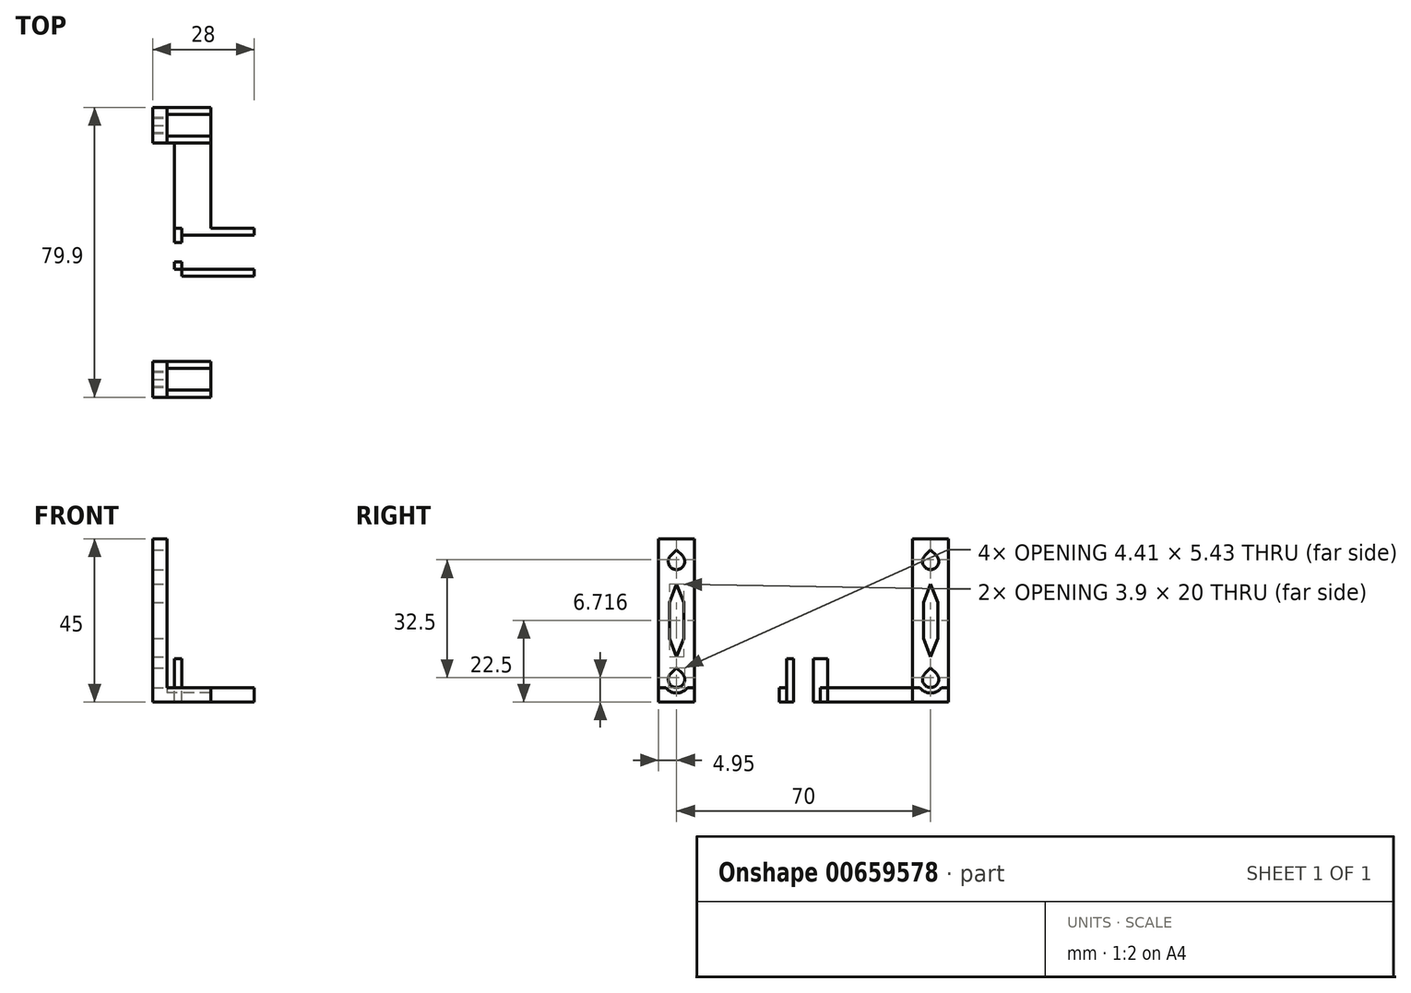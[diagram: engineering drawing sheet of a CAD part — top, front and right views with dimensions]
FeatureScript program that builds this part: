
annotation { "Feature Type Name" : "Feature", "Feature Type Description" : "" }
export const myFeature = defineFeature(function(context is Context, id is Id, definition is map)
    precondition{}
    {
        {
            var Q0;
            Q0=qCreatedBy(makeId("Right.planeOp"),FACE);
            var sketch = newSketch(context, id + "F0", { "sketchPlane" : qUnion([Q0])});
            skLineSegment(sketch, "E0.bottom", {"start": v(4.95, 6.25) * mm, "end": v(-4.95, 6.25) * mm});
            skLineSegment(sketch, "E0.top", {"start": v(4.95, -6.25) * mm, "end": v(-4.95, -6.25) * mm});
            skLineSegment(sketch, "E0.left", {"start": v(4.95, 6.25) * mm, "end": v(4.95, -6.25) * mm});
            skLineSegment(sketch, "E0.right", {"start": v(-4.95, 6.25) * mm, "end": v(-4.95, -6.25) * mm});
            skPoint(sketch, "E0.middle", {"position": v(0, 0) * mm});
            skCircle(sketch, "E1", {"center": v(0, 0) * mm, "radius": 2.25 * mm});
            skLineSegment(sketch, "E2", {"start": v(-4.95, 6.25) * mm, "end": v(-4.95, 16.25) * mm});
            skLineSegment(sketch, "E3", {"start": v(-4.95, 16.25) * mm, "end": v(-1.95, 16.25) * mm});
            skLineSegment(sketch, "E4", {"start": v(-1.95, 16.25) * mm, "end": v(-1.95, 6.25) * mm});
            skLineSegment(sketch, "E5", {"start": v(4.95, 6.25) * mm, "end": v(4.95, 16.25) * mm});
            skLineSegment(sketch, "E6", {"start": v(4.95, 16.25) * mm, "end": v(1.95, 16.25) * mm});
            skLineSegment(sketch, "E7", {"start": v(1.95, 16.25) * mm, "end": v(1.95, 6.25) * mm});
            skLineSegment(sketch, "E8", {"start": v(-4.95, -6.25) * mm, "end": v(-4.95, -2.25) * mm});
            skLineSegment(sketch, "E9", {"start": v(-4.95, -2.25) * mm, "end": v(4.95, -2.25) * mm});
            skLineSegment(sketch, "E10", {"start": v(4.95, -2.25) * mm, "end": v(4.95, -6.25) * mm});
            skLineSegment(sketch, "E11", {"start": v(0, 0) * mm, "end": v(35, 0) * mm});
            skPoint(sketch, "E11.endSnap0", {"position": v(4.95, 0) * mm});
            skCircle(sketch, "E12", {"center": v(0, 0) * mm, "radius": 3.75 * mm});
            skLineSegment(sketch, "E13", {"start": v(1.95, 11.25) * mm, "end": v(0, 6.25) * mm});
            skLineSegment(sketch, "E14", {"start": v(0, 6.25) * mm, "end": v(-1.95, 11.25) * mm});
            skSolve(sketch);
        }
        {
            var Q0;
            Q0=makeQuery(id+"F0.imprint","IMPRINT",FACE,{"disambiguationData":[TD([[makeQuery(id+"F0.imprint","IMPRINT",EDGE,{"derivedFrom":sQuery(id+"F0.wireOp",EDGE,"E0.bottom")}),1.0]])]});
            var Q1;
            {var subQ0=sQuery(id+"F0.wireOp",EDGE,"E2");Q1=makeQuery(id+"F0.imprint","IMPRINT",FACE,{"disambiguationData":[TD([[makeQuery(id+"F0.imprint","IMPRINT",EDGE,{"derivedFrom":subQ0}),-1.0]])]});}
            var Q2;
            {var subQ0=sQuery(id+"F0.wireOp",EDGE,"E5");Q2=makeQuery(id+"F0.imprint","IMPRINT",FACE,{"disambiguationData":[TD([[makeQuery(id+"F0.imprint","IMPRINT",EDGE,{"derivedFrom":subQ0}),1.0]])]});}
            var Q3;
            Q3=makeQuery(id+"F0.imprint","IMPRINT",FACE,{"disambiguationData":[TD([[makeQuery(id+"F0.imprint","IMPRINT",EDGE,{"derivedFrom":sQuery(id+"F0.wireOp",EDGE,"E0.top")}),-1.0]])]});
            var Q4;
            {var subQ1=sQuery(id+"F0.wireOp",EDGE,"E0.left");var subQ3=sQuery(id+"F0.wireOp",EDGE,"E11");var subQ4=makeQuery(id+"F0.imprint","INTERSECT",VERTEX,{"derivedFrom":[subQ1,subQ3]});Q4=makeQuery(id+"F0.imprint","IMPRINT",FACE,{"disambiguationData":[TD([[makeQuery(id+"F0.imprint","IMPRINT",EDGE,{"disambiguationData":[TD([[subQ4,1.0]])],"derivedFrom":subQ3}),-1.0]])]});}
            var Q5;
            {var subQ0=sQuery(id+"F0.wireOp",EDGE,"E9");var subQ1=makeQuery(id+"F0.imprint","INTERSECT",VERTEX,{"derivedFrom":[sQuery(id+"F0.wireOp",EDGE,"E1"),subQ0]});Q5=makeQuery(id+"F0.imprint","IMPRINT",FACE,{"disambiguationData":[TD([[makeQuery(id+"F0.imprint","IMPRINT",EDGE,{"disambiguationData":[TD([[subQ1,1.0]])],"derivedFrom":subQ0}),-1.0]])]});}
            var Q6;
            {var subQ0=sQuery(id+"F0.wireOp",EDGE,"E11");var subQ1=sQuery(id+"F0.wireOp",EDGE,"E1");var subQ2=makeQuery(id+"F0.imprint","INTERSECT",VERTEX,{"derivedFrom":[subQ1,subQ0]});Q6=makeQuery(id+"F0.imprint","IMPRINT",FACE,{"disambiguationData":[TD([[makeQuery(id+"F0.imprint","IMPRINT",EDGE,{"disambiguationData":[TD([[subQ2,-1.0]])],"derivedFrom":subQ1}),-1.0]])]});}
            var Q7;
            {var subQ0=sQuery(id+"F0.wireOp",EDGE,"E11");var subQ1=sQuery(id+"F0.wireOp",EDGE,"E1");var subQ2=makeQuery(id+"F0.imprint","INTERSECT",VERTEX,{"derivedFrom":[subQ1,subQ0]});Q7=makeQuery(id+"F0.imprint","IMPRINT",FACE,{"disambiguationData":[TD([[makeQuery(id+"F0.imprint","IMPRINT",EDGE,{"disambiguationData":[TD([[subQ2,1.0]])],"derivedFrom":subQ1}),-1.0]])]});}
            var Q8;
            {var subQ3=sQuery(id+"F0.wireOp",EDGE,"E14");Q8=makeQuery(id+"F0.imprint","IMPRINT",FACE,{"disambiguationData":[TD([[makeQuery(id+"F0.imprint","IMPRINT",EDGE,{"derivedFrom":subQ3}),1.0]])]});}
            var Q9;
            {var subQ3=sQuery(id+"F0.wireOp",EDGE,"E13");Q9=makeQuery(id+"F0.imprint","IMPRINT",FACE,{"disambiguationData":[TD([[makeQuery(id+"F0.imprint","IMPRINT",EDGE,{"derivedFrom":subQ3}),1.0]])]});}
            extrude(context, id + "F1", {"entities" : qUnion([Q0, Q1, Q2, Q3, Q4, Q5, Q6, Q7, Q8, Q9]), "oppositeDirection" : true, "depth" : 4 * mm, "offsetDistance" : 25 * mm});
        }
        {
            var Q0;
            Q0=makeQuery(id+"F0.imprint","IMPRINT",FACE,{"disambiguationData":[TD([[makeQuery(id+"F0.imprint","IMPRINT",EDGE,{"derivedFrom":sQuery(id+"F0.wireOp",EDGE,"E0.top")}),-1.0]])]});
            extrude(context, id + "F2", {"entities" : qUnion([Q0]), "depth" : 12 * mm, "offsetDistance" : 25 * mm});
        }
        {
            var Q0;
            Q0=makeQuery(id+"F1.opExtrude","SWEPT_FACE",FACE,{"disambiguationData":[OSD([sQuery(id+"F0.wireOp",EDGE,"E6")])]});
            cPlane(context, id + "F3", {"entities" : qUnion([Q0]), "cplaneType" : CPlaneType.OFFSET, "offset" : 0 * mm, "width" : 150 * mm, "height" : 150 * mm});
        }
        {
            var Q0;
            Q0=makeQuery(id+"F1.opExtrude","SWEPT_BODY",BODY,{"disambiguationData":[OSD([sQuery(id+"F0.wireOp",EDGE,"E0.bottom"),sQuery(id+"F0.wireOp",EDGE,"E0.top"),sQuery(id+"F0.wireOp",EDGE,"E0.left"),sQuery(id+"F0.wireOp",EDGE,"E0.right"),sQuery(id+"F0.wireOp",EDGE,"E1"),sQuery(id+"F0.wireOp",EDGE,"E2"),sQuery(id+"F0.wireOp",EDGE,"E3"),sQuery(id+"F0.wireOp",EDGE,"E4"),sQuery(id+"F0.wireOp",EDGE,"E5"),sQuery(id+"F0.wireOp",EDGE,"E6"),sQuery(id+"F0.wireOp",EDGE,"E7"),sQuery(id+"F0.wireOp",EDGE,"E8"),sQuery(id+"F0.wireOp",EDGE,"E10")])]});
            var Q1;
            Q1=qCreatedBy(id+"F3.planeOp",FACE);
            mirror(context, id + "F4", {"operationType" : NewBodyOperationType.ADD, "entities" : qUnion([Q0]), "mirrorPlane" : qUnion([Q1])});
        }
        {
            var Q0;
            Q0=sQuery(id+"F0.wireOp",VERTEX,"E11.end");
            var Q1;
            Q1=sQuery(id+"F0.wireOp",EDGE,"E11");
            cPlane(context, id + "F5", {"entities" : qUnion([Q0, Q1]), "cplaneType" : CPlaneType.LINE_POINT, "offset" : 25 * mm, "width" : 150 * mm, "height" : 150 * mm});
        }
        {
            var Q0;
            Q0=makeQuery(id+"F1.opExtrude","SWEPT_BODY",BODY,{"disambiguationData":[OSD([sQuery(id+"F0.wireOp",EDGE,"E0.bottom"),sQuery(id+"F0.wireOp",EDGE,"E0.top"),sQuery(id+"F0.wireOp",EDGE,"E0.left"),sQuery(id+"F0.wireOp",EDGE,"E0.right"),sQuery(id+"F0.wireOp",EDGE,"E1"),sQuery(id+"F0.wireOp",EDGE,"E2"),sQuery(id+"F0.wireOp",EDGE,"E3"),sQuery(id+"F0.wireOp",EDGE,"E4"),sQuery(id+"F0.wireOp",EDGE,"E5"),sQuery(id+"F0.wireOp",EDGE,"E6"),sQuery(id+"F0.wireOp",EDGE,"E7"),sQuery(id+"F0.wireOp",EDGE,"E8"),sQuery(id+"F0.wireOp",EDGE,"E10")])]});
            var Q1;
            Q1=makeQuery(id+"F2.opExtrude","SWEPT_BODY",BODY,{"disambiguationData":[OSD([sQuery(id+"F0.wireOp",EDGE,"E0.top"),sQuery(id+"F0.wireOp",EDGE,"E8"),sQuery(id+"F0.wireOp",EDGE,"E9"),sQuery(id+"F0.wireOp",EDGE,"E10")])]});
            var Q2;
            Q2=qCreatedBy(id+"F5.planeOp",FACE);
            mirror(context, id + "F6", {"entities" : qUnion([Q0, Q1]), "mirrorPlane" : qUnion([Q2])});
        }
        {
            var Q0;
            Q0=makeQuery(id+"F2.opExtrude","SWEPT_FACE",FACE,{"disambiguationData":[OSD([sQuery(id+"F0.wireOp",EDGE,"E9")])]});
            var sketch = newSketch(context, id + "F7", { "sketchPlane" : qUnion([Q0])});
            skPoint(sketch, "E15.0", {"position": v(0, 4.95) * mm});
            skPoint(sketch, "E16.0", {"position": v(0, 65.05) * mm});
            skPoint(sketch, "E17.0", {"position": v(12, 65.05) * mm});
            skPoint(sketch, "E18.0", {"position": v(12, 4.95) * mm});
            skLineSegment(sketch, "E19", {"start": v(0, 4.95) * mm, "end": v(2, 4.95) * mm});
            skLineSegment(sketch, "E20", {"start": v(2, 4.95) * mm, "end": v(2, 65.05) * mm});
            skLineSegment(sketch, "E21", {"start": v(2, 35) * mm, "end": v(2, 41.65) * mm});
            skLineSegment(sketch, "E22", {"start": v(2, 41.65) * mm, "end": v(2, 28.35) * mm});
            skLineSegment(sketch, "E23", {"start": v(2, 28.35) * mm, "end": v(24, 28.35) * mm});
            skLineSegment(sketch, "E24", {"start": v(24, 28.35) * mm, "end": v(24, 41.65) * mm});
            skLineSegment(sketch, "E25", {"start": v(24, 41.65) * mm, "end": v(2, 41.65) * mm});
            skLineSegment(sketch, "E26", {"start": v(24, 41.65) * mm, "end": v(24, 39.65) * mm});
            skLineSegment(sketch, "E27", {"start": v(24, 39.65) * mm, "end": v(2, 39.65) * mm});
            skLineSegment(sketch, "E28", {"start": v(24, 28.35) * mm, "end": v(24, 30.35) * mm});
            skLineSegment(sketch, "E29", {"start": v(24, 30.35) * mm, "end": v(2, 30.35) * mm});
            skLineSegment(sketch, "E30", {"start": v(2, 28.35) * mm, "end": v(4, 28.35) * mm});
            skLineSegment(sketch, "E31", {"start": v(4, 28.35) * mm, "end": v(4, 41.65) * mm});
            skLineSegment(sketch, "E32", {"start": v(2, 35) * mm, "end": v(2, 37.7) * mm});
            skLineSegment(sketch, "E33", {"start": v(2, 37.7) * mm, "end": v(4, 37.7) * mm});
            skLineSegment(sketch, "E34", {"start": v(2, 35) * mm, "end": v(2, 32.3) * mm});
            skLineSegment(sketch, "E35", {"start": v(2, 32.3) * mm, "end": v(4, 32.3) * mm});
            skLineSegment(sketch, "E36", {"start": v(12, 4.95) * mm, "end": v(12, 28.35) * mm});
            skPoint(sketch, "E36.endSnap0", {"position": v(13, 28.35) * mm});
            skLineSegment(sketch, "E37", {"start": v(12, 65.05) * mm, "end": v(12, 41.65) * mm});
            skPoint(sketch, "E37.endSnap0", {"position": v(13, 41.65) * mm});
            skLineSegment(sketch, "E38", {"start": v(12, 65.05) * mm, "end": v(2, 65.05) * mm});
            skSolve(sketch);
        }
        {
            var Q0;
            {var subQ1=sQuery(id+"F7.wireOp",EDGE,"E30");Q0=makeQuery(id+"F7.imprint","IMPRINT",FACE,{"disambiguationData":[TD([[makeQuery(id+"F7.imprint","IMPRINT",EDGE,{"derivedFrom":subQ1}),-1.0]])]});}
            var Q1;
            {var subQ0=sQuery(id+"F7.wireOp",EDGE,"E28");Q1=makeQuery(id+"F7.imprint","IMPRINT",FACE,{"disambiguationData":[TD([[makeQuery(id+"F7.imprint","IMPRINT",EDGE,{"derivedFrom":subQ0}),1.0]])]});}
            var Q2;
            {var subQ0=sQuery(id+"F7.wireOp",EDGE,"E30");Q2=makeQuery(id+"F7.imprint","IMPRINT",FACE,{"disambiguationData":[TD([[makeQuery(id+"F7.imprint","IMPRINT",EDGE,{"derivedFrom":subQ0}),1.0]])]});}
            var Q3;
            {var subQ3=sQuery(id+"F7.wireOp",EDGE,"E35");Q3=makeQuery(id+"F7.imprint","IMPRINT",FACE,{"disambiguationData":[TD([[makeQuery(id+"F7.imprint","IMPRINT",EDGE,{"derivedFrom":subQ3}),-1.0]])]});}
            var Q4;
            {var subQ3=sQuery(id+"F7.wireOp",EDGE,"E33");Q4=makeQuery(id+"F7.imprint","IMPRINT",FACE,{"disambiguationData":[TD([[makeQuery(id+"F7.imprint","IMPRINT",EDGE,{"derivedFrom":subQ3}),1.0]])]});}
            var Q5;
            {var subQ1=sQuery(id+"F7.wireOp",EDGE,"E22");var subQ3=sQuery(id+"F7.wireOp",EDGE,"E27");var subQ4=makeQuery(id+"F7.imprint","INTERSECT",VERTEX,{"derivedFrom":[subQ1,subQ3]});Q5=makeQuery(id+"F7.imprint","IMPRINT",FACE,{"disambiguationData":[TD([[makeQuery(id+"F7.imprint","IMPRINT",EDGE,{"disambiguationData":[TD([[subQ4,1.0]])],"derivedFrom":subQ3}),-1.0]])]});}
            var Q6;
            {var subQ1=sQuery(id+"F7.wireOp",EDGE,"E26");Q6=makeQuery(id+"F7.imprint","IMPRINT",FACE,{"disambiguationData":[TD([[makeQuery(id+"F7.imprint","IMPRINT",EDGE,{"derivedFrom":subQ1}),-1.0]])]});}
            var Q7;
            {var subQ0=sQuery(id+"F7.wireOp",EDGE,"E37");Q7=makeQuery(id+"F7.imprint","IMPRINT",FACE,{"disambiguationData":[TD([[makeQuery(id+"F7.imprint","IMPRINT",EDGE,{"derivedFrom":subQ0}),-1.0]])]});}
            var Q8;
            {var subQ4=sQuery(id+"F7.wireOp",EDGE,"E24");Q8=makeQuery(id+"F7.imprint","IMPRINT",FACE,{"disambiguationData":[TD([[makeQuery(id+"F7.imprint","IMPRINT",EDGE,{"derivedFrom":subQ4}),1.0]])]});}
            var Q9;
            Q9=makeQuery(id+"F7.imprint","IMPRINT",FACE,{"disambiguationData":[TD([[makeQuery(id+"F7.imprint","IMPRINT",EDGE,{"derivedFrom":sQuery(id+"F7.wireOp",EDGE,"E32")}),-1.0]])]});
            extrude(context, id + "F8", {"entities" : qUnion([Q0, Q1, Q2, Q3, Q4, Q5, Q6, Q7, Q8, Q9]), "oppositeDirection" : true, "depth" : 4 * mm, "offsetDistance" : 25 * mm});
        }
        {
            var Q0;
            {var subQ1=sQuery(id+"F7.wireOp",EDGE,"E26");Q0=makeQuery(id+"F7.imprint","IMPRINT",FACE,{"disambiguationData":[TD([[makeQuery(id+"F7.imprint","IMPRINT",EDGE,{"derivedFrom":subQ1}),-1.0]])]});}
            var Q1;
            {var subQ1=sQuery(id+"F7.wireOp",EDGE,"E22");var subQ3=sQuery(id+"F7.wireOp",EDGE,"E27");var subQ4=makeQuery(id+"F7.imprint","INTERSECT",VERTEX,{"derivedFrom":[subQ1,subQ3]});Q1=makeQuery(id+"F7.imprint","IMPRINT",FACE,{"disambiguationData":[TD([[makeQuery(id+"F7.imprint","IMPRINT",EDGE,{"disambiguationData":[TD([[subQ4,1.0]])],"derivedFrom":subQ3}),-1.0]])]});}
            var Q2;
            {var subQ3=sQuery(id+"F7.wireOp",EDGE,"E33");Q2=makeQuery(id+"F7.imprint","IMPRINT",FACE,{"disambiguationData":[TD([[makeQuery(id+"F7.imprint","IMPRINT",EDGE,{"derivedFrom":subQ3}),1.0]])]});}
            var Q3;
            {var subQ3=sQuery(id+"F7.wireOp",EDGE,"E35");Q3=makeQuery(id+"F7.imprint","IMPRINT",FACE,{"disambiguationData":[TD([[makeQuery(id+"F7.imprint","IMPRINT",EDGE,{"derivedFrom":subQ3}),-1.0]])]});}
            var Q4;
            {var subQ0=sQuery(id+"F7.wireOp",EDGE,"E30");Q4=makeQuery(id+"F7.imprint","IMPRINT",FACE,{"disambiguationData":[TD([[makeQuery(id+"F7.imprint","IMPRINT",EDGE,{"derivedFrom":subQ0}),1.0]])]});}
            var Q5;
            {var subQ0=sQuery(id+"F7.wireOp",EDGE,"E28");Q5=makeQuery(id+"F7.imprint","IMPRINT",FACE,{"disambiguationData":[TD([[makeQuery(id+"F7.imprint","IMPRINT",EDGE,{"derivedFrom":subQ0}),1.0]])]});}
            extrude(context, id + "F9", {"entities" : qUnion([Q0, Q1, Q2, Q3, Q4, Q5]), "operationType" : NewBodyOperationType.ADD, "depth" : 8 * mm, "offsetDistance" : 25 * mm});
        }
        {
            var Q0;
            Q0=qCreatedBy(makeId("Right.planeOp"),FACE);
            var sketch = newSketch(context, id + "F10", { "sketchPlane" : qUnion([Q0])});
            skPoint(sketch, "E39.0", {"position": v(0, 0) * mm});
            skLineSegment(sketch, "E40.0", {"start": v(4.95, 16.25) * mm, "end": v(1.95, 16.25) * mm});
            skPoint(sketch, "E41.0", {"position": v(35, -2.25) * mm});
            skLineSegment(sketch, "E42", {"start": v(35, -2.25) * mm, "end": v(35, 7.75) * mm});
            skPoint(sketch, "E43.MirrorP", {"position": v(0, 32.5) * mm});
            skPoint(sketch, "E44.MirrorP", {"position": v(70, 0) * mm});
            skPoint(sketch, "E45.MirrorP", {"position": v(70, 32.5) * mm});
            skLineSegment(sketch, "E46", {"start": v(0, 0) * mm, "end": v(0, 2.25) * mm});
            skLineSegment(sketch, "E47", {"start": v(0, 0) * mm, "end": v(2.25, 0) * mm});
            skLineSegment(sketch, "E48", {"start": v(2.25, 0) * mm, "end": v(0, 2.25) * mm});
            skLineSegment(sketch, "E49", {"start": v(0, 0) * mm, "end": v(1.6, 1.6) * mm});
            skLineSegment(sketch, "E50", {"start": v(1.6, 1.6) * mm, "end": v(0, 3.18) * mm});
            skLineSegment(sketch, "E51", {"start": v(0, 3.18) * mm, "end": v(-1.6, 1.6) * mm});
            skCircle(sketch, "E52.0", {"center": v(0, 0) * mm, "radius": 2.25 * mm});
            skCircle(sketch, "E53.0", {"center": v(0, 32.5) * mm, "radius": 2.25 * mm});
            skCircle(sketch, "E54.0", {"center": v(70, 0) * mm, "radius": 2.25 * mm});
            skCircle(sketch, "E55.0", {"center": v(70, 32.5) * mm, "radius": 2.25 * mm});
            skLineSegment(sketch, "E56", {"start": v(0, 32.5) * mm, "end": v(2.25, 32.5) * mm});
            skLineSegment(sketch, "E57", {"start": v(2.25, 32.5) * mm, "end": v(0, 34.75) * mm});
            skLineSegment(sketch, "E58", {"start": v(0, 34.75) * mm, "end": v(0, 32.5) * mm});
            skLineSegment(sketch, "E59", {"start": v(0, 32.5) * mm, "end": v(1.6, 34.1) * mm});
            skLineSegment(sketch, "E60", {"start": v(1.6, 34.1) * mm, "end": v(0, 35.68) * mm});
            skLineSegment(sketch, "E61", {"start": v(0, 35.68) * mm, "end": v(-1.6, 34.1) * mm});
            skLineSegment(sketch, "E62", {"start": v(70, 32.5) * mm, "end": v(72.25, 32.5) * mm});
            skLineSegment(sketch, "E63", {"start": v(72.25, 32.5) * mm, "end": v(70, 34.75) * mm});
            skLineSegment(sketch, "E64", {"start": v(70, 34.75) * mm, "end": v(70, 32.5) * mm});
            skLineSegment(sketch, "E65", {"start": v(70, 32.5) * mm, "end": v(71.6, 34.1) * mm});
            skLineSegment(sketch, "E66", {"start": v(71.6, 34.1) * mm, "end": v(70, 35.68) * mm});
            skLineSegment(sketch, "E67", {"start": v(70, 35.68) * mm, "end": v(68.4, 34.1) * mm});
            skLineSegment(sketch, "E68", {"start": v(70, 0) * mm, "end": v(72.25, 0) * mm});
            skLineSegment(sketch, "E69", {"start": v(72.25, 0) * mm, "end": v(70, 2.25) * mm});
            skLineSegment(sketch, "E70", {"start": v(70, 2.25) * mm, "end": v(70, 0) * mm});
            skLineSegment(sketch, "E71", {"start": v(70, 0) * mm, "end": v(71.6, 1.6) * mm});
            skLineSegment(sketch, "E72", {"start": v(71.6, 1.6) * mm, "end": v(70, 3.18) * mm});
            skLineSegment(sketch, "E73", {"start": v(70, 3.18) * mm, "end": v(68.4, 1.6) * mm});
            skSolve(sketch);
        }
        {
            var Q0;
            {var subQ2=sQuery(id+"F10.wireOp",EDGE,"E60");Q0=makeQuery(id+"F10.imprint","IMPRINT",FACE,{"disambiguationData":[TD([[makeQuery(id+"F10.imprint","IMPRINT",EDGE,{"derivedFrom":subQ2}),1.0]])]});}
            var Q1;
            {var subQ0=sQuery(id+"F10.wireOp",EDGE,"E50");Q1=makeQuery(id+"F10.imprint","IMPRINT",FACE,{"disambiguationData":[TD([[makeQuery(id+"F10.imprint","IMPRINT",EDGE,{"derivedFrom":subQ0}),1.0]])]});}
            var Q2;
            {var subQ2=sQuery(id+"F10.wireOp",EDGE,"E72");Q2=makeQuery(id+"F10.imprint","IMPRINT",FACE,{"disambiguationData":[TD([[makeQuery(id+"F10.imprint","IMPRINT",EDGE,{"derivedFrom":subQ2}),1.0]])]});}
            var Q3;
            {var subQ2=sQuery(id+"F10.wireOp",EDGE,"E66");Q3=makeQuery(id+"F10.imprint","IMPRINT",FACE,{"disambiguationData":[TD([[makeQuery(id+"F10.imprint","IMPRINT",EDGE,{"derivedFrom":subQ2}),1.0]])]});}
            extrude(context, id + "F11", {"entities" : qUnion([Q0, Q1, Q2, Q3]), "operationType" : NewBodyOperationType.REMOVE, "oppositeDirection" : true, "depth" : 4 * mm, "offsetDistance" : 25 * mm});
        }
    });
